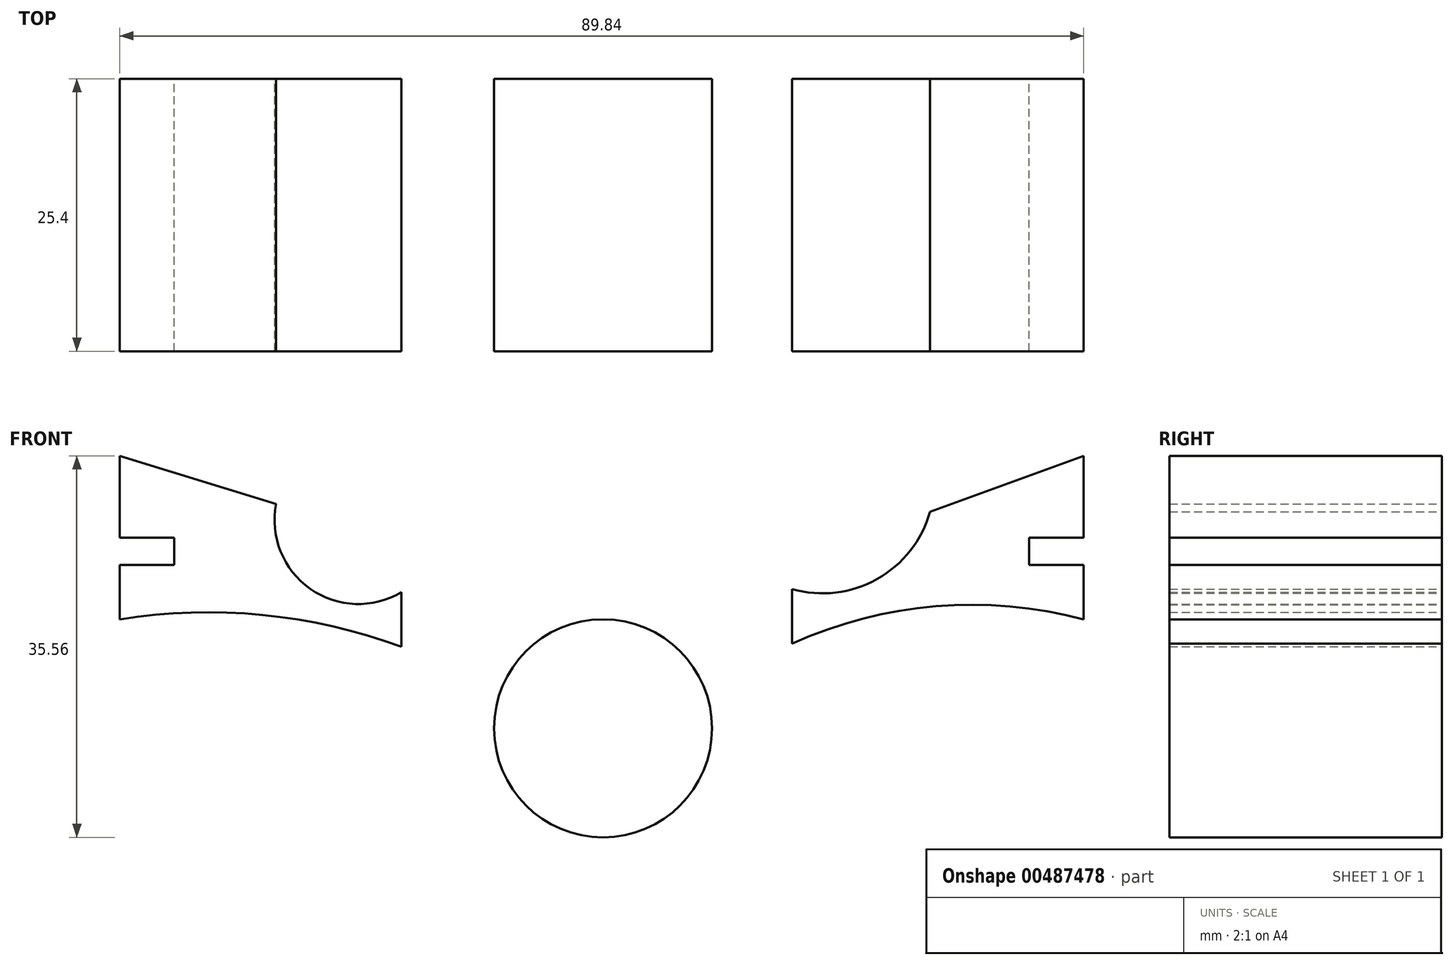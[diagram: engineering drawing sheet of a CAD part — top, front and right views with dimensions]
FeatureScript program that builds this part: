
annotation { "Feature Type Name" : "Feature", "Feature Type Description" : "" }
export const myFeature = defineFeature(function(context is Context, id is Id, definition is map)
    precondition{}
    {
        {
            var Q0;
            Q0=qCreatedBy(makeId("Front.planeOp"),FACE);
            var sketch = newSketch(context, id + "F0", { "sketchPlane" : qUnion([Q0])});
            skCircle(sketch, "E0", {"center": v(0, 0) * mm, "radius": 10.16 * mm});
            skLineSegment(sketch, "E1", {"start": v(-30.48, 20.9) * mm, "end": v(-45.04, 25.4) * mm});
            skLineSegment(sketch, "E2", {"start": v(30.48, 20.2) * mm, "end": v(44.8, 25.4) * mm});
            skArc(sketch, "E3", {"start": v(-30.48, 20.9) * mm, "mid": v(-27.3, 13.01) * mm, "end": v(-18.8, 12.68) * mm});
            skArc(sketch, "E4", {"start": v(17.63, 12.97) * mm, "mid": v(25.56, 13.91) * mm, "end": v(30.48, 20.2) * mm});
            skLineSegment(sketch, "E5", {"start": v(-18.8, 12.68) * mm, "end": v(-18.8, 7.6) * mm});
            skLineSegment(sketch, "E6", {"start": v(17.63, 12.97) * mm, "end": v(17.63, 7.89) * mm});
            skLineSegment(sketch, "E7", {"start": v(-45.04, 25.4) * mm, "end": v(-45.04, 17.78) * mm});
            skLineSegment(sketch, "E8", {"start": v(44.8, 25.4) * mm, "end": v(44.8, 17.78) * mm});
            skLineSegment(sketch, "E9", {"start": v(44.8, 17.78) * mm, "end": v(39.72, 17.78) * mm});
            skLineSegment(sketch, "E10", {"start": v(-45.04, 17.78) * mm, "end": v(-39.96, 17.78) * mm});
            skLineSegment(sketch, "E11", {"start": v(-39.96, 17.78) * mm, "end": v(-39.96, 15.24) * mm});
            skLineSegment(sketch, "E12", {"start": v(-39.96, 15.24) * mm, "end": v(-45.04, 15.24) * mm});
            skLineSegment(sketch, "E13", {"start": v(-45.04, 15.24) * mm, "end": v(-45.04, 10.16) * mm});
            skLineSegment(sketch, "E14", {"start": v(39.72, 17.78) * mm, "end": v(39.72, 15.24) * mm});
            skLineSegment(sketch, "E15", {"start": v(39.72, 15.24) * mm, "end": v(44.8, 15.24) * mm});
            skLineSegment(sketch, "E16", {"start": v(44.8, 15.24) * mm, "end": v(44.8, 10.16) * mm});
            skArc(sketch, "E17", {"start": v(-18.8, 7.6) * mm, "mid": v(-31.76, 10.57) * mm, "end": v(-45.04, 10.16) * mm});
            skArc(sketch, "E18", {"start": v(44.8, 10.16) * mm, "mid": v(31.02, 11.38) * mm, "end": v(17.63, 7.89) * mm});
            skSolve(sketch);
        }
        {
            var Q0;
            Q0=makeQuery(id+"F0.imprint","IMPRINT",FACE,{"disambiguationData":[TD([[makeQuery(id+"F0.imprint","IMPRINT",EDGE,{"derivedFrom":sQuery(id+"F0.wireOp",EDGE,"E1")}),1.0]])]});
            var Q1;
            Q1=makeQuery(id+"F0.imprint","IMPRINT",FACE,{"disambiguationData":[TD([[makeQuery(id+"F0.imprint","IMPRINT",EDGE,{"derivedFrom":sQuery(id+"F0.wireOp",EDGE,"E2")}),-1.0]])]});
            var Q2;
            Q2=makeQuery(id+"F0.imprint","IMPRINT",FACE,{"disambiguationData":[TD([[makeQuery(id+"F0.imprint","IMPRINT",EDGE,{"derivedFrom":sQuery(id+"F0.wireOp",EDGE,"E0")}),1.0]])]});
            extrude(context, id + "F1", {"entities" : qUnion([Q0, Q1, Q2]), "depth" : 25.4 * mm});
        }
    });
